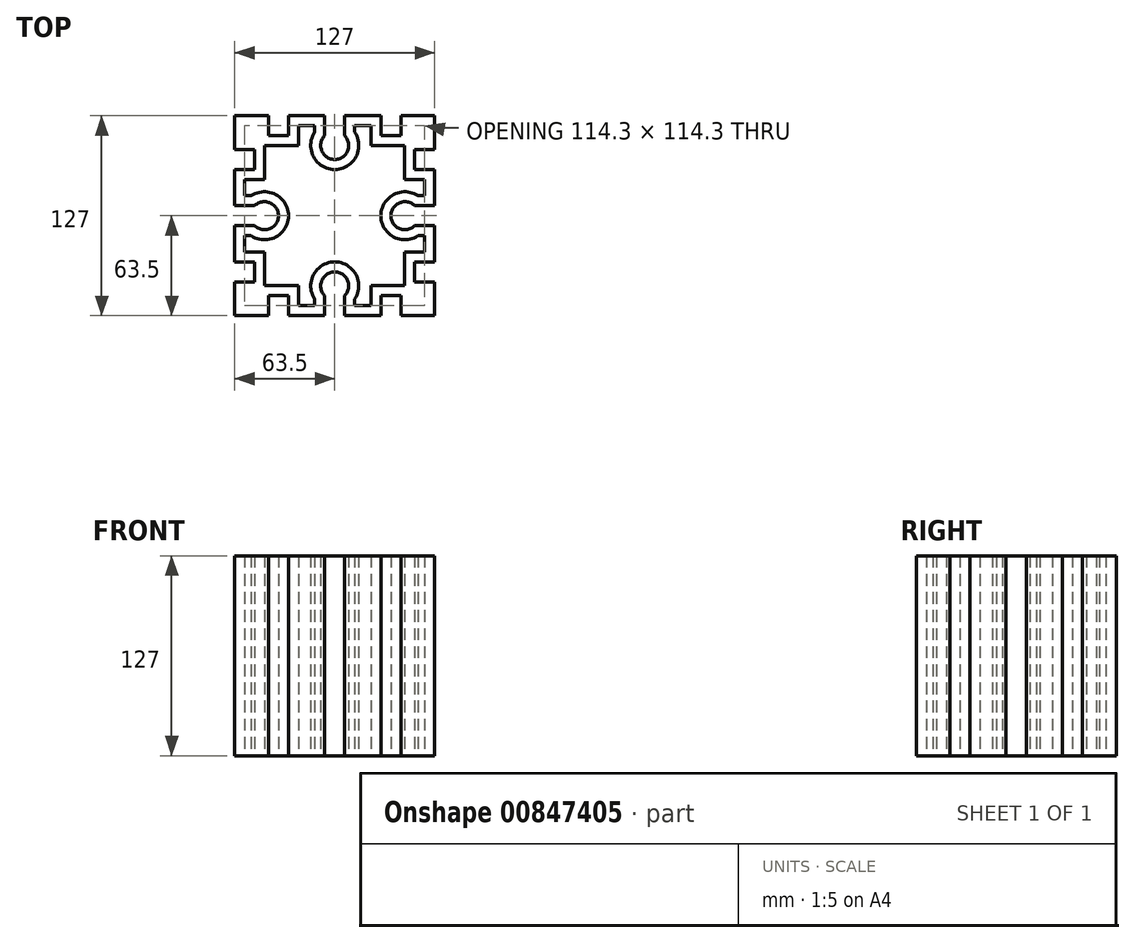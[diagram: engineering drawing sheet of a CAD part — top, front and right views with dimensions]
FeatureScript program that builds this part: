
annotation { "Feature Type Name" : "Feature", "Feature Type Description" : "" }
export const myFeature = defineFeature(function(context is Context, id is Id, definition is map)
    precondition{}
    {
        {
            var Q0;
            Q0=qCreatedBy(makeId("Top.planeOp"),FACE);
            var sketch = newSketch(context, id + "F0", { "sketchPlane" : qUnion([Q0])});
            skLineSegment(sketch, "E0.bottom", {"start": v(-63.5, 63.5) * mm, "end": v(-42.1, 63.5) * mm});
            skLineSegment(sketch, "E0.top", {"start": v(-29.4, -63.5) * mm, "end": v(-6.35, -63.5) * mm});
            skLineSegment(sketch, "E0.right", {"start": v(63.5, 63.5) * mm, "end": v(63.5, 42.1) * mm});
            skPoint(sketch, "E0.middle", {"position": v(0, 0) * mm});
            skLineSegment(sketch, "E1.left", {"start": v(6.35, 50.8) * mm, "end": v(6.35, 63.5) * mm});
            skLineSegment(sketch, "E1.right", {"start": v(-6.35, 50.8) * mm, "end": v(-6.35, 63.5) * mm});
            skPoint(sketch, "E1.middle", {"position": v(0, 63.5) * mm});
            skLineSegment(sketch, "E2.bottom", {"start": v(-29.4, 50.8) * mm, "end": v(-42.1, 50.8) * mm});
            skLineSegment(sketch, "E2.left", {"start": v(-29.4, 50.8) * mm, "end": v(-29.4, 63.5) * mm});
            skLineSegment(sketch, "E2.right", {"start": v(-42.1, 50.8) * mm, "end": v(-42.1, 63.5) * mm});
            skPoint(sketch, "E2.middle", {"position": v(-35.75, 63.5) * mm});
            skPoint(sketch, "E3.MirrorP", {"position": v(0, 127) * mm});
            skLineSegment(sketch, "E4.MirrorCS", {"start": v(29.4, 50.8) * mm, "end": v(42.1, 50.8) * mm});
            skPoint(sketch, "E5.MirrorP", {"position": v(35.75, 63.5) * mm});
            skLineSegment(sketch, "E6.MirrorCS", {"start": v(29.4, 50.8) * mm, "end": v(29.4, 63.5) * mm});
            skLineSegment(sketch, "E7.MirrorCS", {"start": v(42.1, 50.8) * mm, "end": v(42.1, 63.5) * mm});
            skPoint(sketch, "E8.MirrorCS.end.orphan", {"position": v(42.1, 76.2) * mm});
            skPoint(sketch, "E9.orphan", {"position": v(29.4, 76.2) * mm});
            skPoint(sketch, "E1.top.start.orphan", {"position": v(6.35, 76.2) * mm});
            skPoint(sketch, "E10.orphan", {"position": v(-6.35, 76.2) * mm});
            skPoint(sketch, "E11.orphan", {"position": v(-29.4, 76.2) * mm});
            skPoint(sketch, "E12.orphan", {"position": v(-42.1, 76.2) * mm});
            skLineSegment(sketch, "E13.trimOffspring", {"start": v(-29.4, 63.5) * mm, "end": v(-6.35, 63.5) * mm});
            skLineSegment(sketch, "E14.trimOffspring", {"start": v(6.35, 63.5) * mm, "end": v(29.4, 63.5) * mm});
            skLineSegment(sketch, "E15.trimOffspring", {"start": v(42.1, 63.5) * mm, "end": v(63.5, 63.5) * mm});
            skArc(sketch, "E16", {"start": v(-6.35, 50.8) * mm, "mid": v(0, 35.69) * mm, "end": v(6.35, 50.8) * mm});
            skPoint(sketch, "E17.1.0", {"position": v(-76.2, 6.35) * mm});
            skPoint(sketch, "E17.1.1", {"position": v(-76.2, -29.4) * mm});
            skPoint(sketch, "E17.1.2", {"position": v(-76.2, -6.35) * mm});
            skLineSegment(sketch, "E17.1.3", {"start": v(-50.8, 29.4) * mm, "end": v(-50.8, 42.1) * mm});
            skLineSegment(sketch, "E17.1.4", {"start": v(-50.8, -6.35) * mm, "end": v(-63.5, -6.35) * mm});
            skPoint(sketch, "E17.1.5", {"position": v(-76.2, -42.1) * mm});
            skLineSegment(sketch, "E17.1.6", {"start": v(-50.8, 29.4) * mm, "end": v(-63.5, 29.4) * mm});
            skArc(sketch, "E17.1.7", {"start": v(-50.8, -6.35) * mm, "mid": v(-35.69, 0) * mm, "end": v(-50.8, 6.35) * mm});
            skLineSegment(sketch, "E17.1.10", {"start": v(-50.8, 6.35) * mm, "end": v(-63.5, 6.35) * mm});
            skPoint(sketch, "E17.1.11", {"position": v(-76.2, 29.4) * mm});
            skLineSegment(sketch, "E17.1.12", {"start": v(-50.8, -29.4) * mm, "end": v(-63.5, -29.4) * mm});
            skPoint(sketch, "E17.1.13", {"position": v(-76.2, 42.1) * mm});
            skLineSegment(sketch, "E17.1.14", {"start": v(-50.8, 42.1) * mm, "end": v(-63.5, 42.1) * mm});
            skPoint(sketch, "E17.1.15", {"position": v(-63.5, 0) * mm});
            skLineSegment(sketch, "E17.1.16", {"start": v(-50.8, -29.4) * mm, "end": v(-50.8, -42.1) * mm});
            skLineSegment(sketch, "E17.1.17", {"start": v(-50.8, -42.1) * mm, "end": v(-63.5, -42.1) * mm});
            skPoint(sketch, "E17.1.18", {"position": v(-63.5, 35.75) * mm});
            skLineSegment(sketch, "E17.1.19", {"start": v(-63.5, 42.1) * mm, "end": v(-63.5, 63.5) * mm});
            skPoint(sketch, "E17.1.20", {"position": v(-63.5, -35.75) * mm});
            skPoint(sketch, "E17.1.21", {"position": v(-76.2, -42.1) * mm});
            skPoint(sketch, "E17.1.22", {"position": v(-63.5, 35.75) * mm});
            skLineSegment(sketch, "E17.1.23", {"start": v(-50.8, -42.1) * mm, "end": v(-63.5, -42.1) * mm});
            skLineSegment(sketch, "E17.1.24", {"start": v(-50.8, -42.1) * mm, "end": v(-63.5, -42.1) * mm});
            skPoint(sketch, "E17.1.25", {"position": v(-76.2, -42.1) * mm});
            skPoint(sketch, "E17.2.0", {"position": v(-6.35, -76.2) * mm});
            skPoint(sketch, "E17.2.1", {"position": v(29.4, -76.2) * mm});
            skPoint(sketch, "E17.2.2", {"position": v(6.35, -76.2) * mm});
            skLineSegment(sketch, "E17.2.3", {"start": v(-29.4, -50.8) * mm, "end": v(-42.1, -50.8) * mm});
            skLineSegment(sketch, "E17.2.4", {"start": v(6.35, -50.8) * mm, "end": v(6.35, -63.5) * mm});
            skPoint(sketch, "E17.2.5", {"position": v(42.1, -76.2) * mm});
            skLineSegment(sketch, "E17.2.6", {"start": v(-29.4, -50.8) * mm, "end": v(-29.4, -63.5) * mm});
            skArc(sketch, "E17.2.7", {"start": v(6.35, -50.8) * mm, "mid": v(0, -35.69) * mm, "end": v(-6.35, -50.8) * mm});
            skLineSegment(sketch, "E17.2.10", {"start": v(-6.35, -50.8) * mm, "end": v(-6.35, -63.5) * mm});
            skPoint(sketch, "E17.2.11", {"position": v(-29.4, -76.2) * mm});
            skLineSegment(sketch, "E17.2.12", {"start": v(29.4, -50.8) * mm, "end": v(29.4, -63.5) * mm});
            skPoint(sketch, "E17.2.13", {"position": v(-42.1, -76.2) * mm});
            skLineSegment(sketch, "E17.2.14", {"start": v(-42.1, -50.8) * mm, "end": v(-42.1, -63.5) * mm});
            skPoint(sketch, "E17.2.15", {"position": v(0, -63.5) * mm});
            skLineSegment(sketch, "E17.2.16", {"start": v(29.4, -50.8) * mm, "end": v(42.1, -50.8) * mm});
            skLineSegment(sketch, "E17.2.17", {"start": v(42.1, -50.8) * mm, "end": v(42.1, -63.5) * mm});
            skPoint(sketch, "E17.2.18", {"position": v(-35.75, -63.5) * mm});
            skLineSegment(sketch, "E17.2.19", {"start": v(-42.1, -63.5) * mm, "end": v(-63.5, -63.5) * mm});
            skPoint(sketch, "E17.2.20", {"position": v(35.75, -63.5) * mm});
            skPoint(sketch, "E17.2.21", {"position": v(42.1, -76.2) * mm});
            skPoint(sketch, "E17.2.22", {"position": v(-35.75, -63.5) * mm});
            skLineSegment(sketch, "E17.2.23", {"start": v(42.1, -50.8) * mm, "end": v(42.1, -63.5) * mm});
            skLineSegment(sketch, "E17.2.24", {"start": v(42.1, -50.8) * mm, "end": v(42.1, -63.5) * mm});
            skPoint(sketch, "E17.2.25", {"position": v(42.1, -76.2) * mm});
            skPoint(sketch, "E17.3.0", {"position": v(76.2, -6.35) * mm});
            skPoint(sketch, "E17.3.1", {"position": v(76.2, 29.4) * mm});
            skPoint(sketch, "E17.3.2", {"position": v(76.2, 6.35) * mm});
            skLineSegment(sketch, "E17.3.3", {"start": v(50.8, -29.4) * mm, "end": v(50.8, -42.1) * mm});
            skLineSegment(sketch, "E17.3.4", {"start": v(50.8, 6.35) * mm, "end": v(63.5, 6.35) * mm});
            skPoint(sketch, "E17.3.5", {"position": v(76.2, 42.1) * mm});
            skLineSegment(sketch, "E17.3.6", {"start": v(50.8, -29.4) * mm, "end": v(63.5, -29.4) * mm});
            skArc(sketch, "E17.3.7", {"start": v(50.8, 6.35) * mm, "mid": v(35.69, 0) * mm, "end": v(50.8, -6.35) * mm});
            skLineSegment(sketch, "E17.3.8", {"start": v(63.5, -6.35) * mm, "end": v(63.5, -29.4) * mm});
            skLineSegment(sketch, "E17.3.9", {"start": v(63.5, 29.4) * mm, "end": v(63.5, 6.35) * mm});
            skLineSegment(sketch, "E17.3.10", {"start": v(50.8, -6.35) * mm, "end": v(63.5, -6.35) * mm});
            skPoint(sketch, "E17.3.11", {"position": v(76.2, -29.4) * mm});
            skLineSegment(sketch, "E17.3.12", {"start": v(50.8, 29.4) * mm, "end": v(63.5, 29.4) * mm});
            skPoint(sketch, "E17.3.13", {"position": v(76.2, -42.1) * mm});
            skLineSegment(sketch, "E17.3.14", {"start": v(50.8, -42.1) * mm, "end": v(63.5, -42.1) * mm});
            skPoint(sketch, "E17.3.15", {"position": v(63.5, 0) * mm});
            skLineSegment(sketch, "E17.3.16", {"start": v(50.8, 29.4) * mm, "end": v(50.8, 42.1) * mm});
            skLineSegment(sketch, "E17.3.17", {"start": v(50.8, 42.1) * mm, "end": v(63.5, 42.1) * mm});
            skPoint(sketch, "E17.3.18", {"position": v(63.5, -35.75) * mm});
            skLineSegment(sketch, "E17.3.19", {"start": v(63.5, -42.1) * mm, "end": v(63.5, -63.5) * mm});
            skPoint(sketch, "E17.3.20", {"position": v(63.5, 35.75) * mm});
            skPoint(sketch, "E17.3.21", {"position": v(76.2, 42.1) * mm});
            skPoint(sketch, "E17.3.22", {"position": v(63.5, -35.75) * mm});
            skLineSegment(sketch, "E17.3.23", {"start": v(50.8, 42.1) * mm, "end": v(63.5, 42.1) * mm});
            skLineSegment(sketch, "E17.3.24", {"start": v(50.8, 42.1) * mm, "end": v(63.5, 42.1) * mm});
            skPoint(sketch, "E17.3.25", {"position": v(76.2, 42.1) * mm});
            skLineSegment(sketch, "E18.trimOffspring", {"start": v(-63.5, 29.4) * mm, "end": v(-63.5, 6.35) * mm});
            skLineSegment(sketch, "E19.trimOffspring", {"start": v(-63.5, -6.35) * mm, "end": v(-63.5, -29.4) * mm});
            skLineSegment(sketch, "E20.trimOffspring", {"start": v(-63.5, -42.1) * mm, "end": v(-63.5, -63.5) * mm});
            skLineSegment(sketch, "E21.trimOffspring", {"start": v(6.35, -63.5) * mm, "end": v(29.4, -63.5) * mm});
            skLineSegment(sketch, "E22.trimOffspring", {"start": v(42.1, -63.5) * mm, "end": v(63.5, -63.5) * mm});
            skLineSegment(sketch, "E23.0", {"start": v(-44.45, 23.05) * mm, "end": v(-44.45, 44.45) * mm});
            skLineSegment(sketch, "E23.1", {"start": v(-44.45, 23.05) * mm, "end": v(-57.15, 23.05) * mm});
            skLineSegment(sketch, "E23.2", {"start": v(-57.15, 23.05) * mm, "end": v(-57.15, 12.7) * mm});
            skLineSegment(sketch, "E23.3", {"start": v(-53, 12.7) * mm, "end": v(-57.15, 12.7) * mm});
            skArc(sketch, "E23.4", {"start": v(-53, -12.7) * mm, "mid": v(-29.34, 0) * mm, "end": v(-53, 12.7) * mm});
            skLineSegment(sketch, "E23.5", {"start": v(-44.45, -23.05) * mm, "end": v(-44.45, -44.45) * mm});
            skLineSegment(sketch, "E23.6", {"start": v(-44.45, -23.05) * mm, "end": v(-57.15, -23.05) * mm});
            skLineSegment(sketch, "E23.7", {"start": v(-57.15, -12.7) * mm, "end": v(-57.15, -23.05) * mm});
            skLineSegment(sketch, "E23.8", {"start": v(-53, -12.7) * mm, "end": v(-57.15, -12.7) * mm});
            skLineSegment(sketch, "E24.1.0", {"start": v(12.7, 53) * mm, "end": v(12.7, 57.15) * mm});
            skArc(sketch, "E24.1.1", {"start": v(-12.7, 53) * mm, "mid": v(0, 29.34) * mm, "end": v(12.7, 53) * mm});
            skLineSegment(sketch, "E24.1.2", {"start": v(-12.7, 53) * mm, "end": v(-12.7, 57.15) * mm});
            skLineSegment(sketch, "E24.1.3", {"start": v(-12.7, 57.15) * mm, "end": v(-23.05, 57.15) * mm});
            skLineSegment(sketch, "E24.1.4", {"start": v(-23.05, 44.45) * mm, "end": v(-23.05, 57.15) * mm});
            skLineSegment(sketch, "E24.1.5", {"start": v(-23.05, 44.45) * mm, "end": v(-44.45, 44.45) * mm});
            skLineSegment(sketch, "E24.1.6", {"start": v(23.05, 57.15) * mm, "end": v(12.7, 57.15) * mm});
            skLineSegment(sketch, "E24.1.7", {"start": v(23.05, 44.45) * mm, "end": v(23.05, 57.15) * mm});
            skLineSegment(sketch, "E24.1.8", {"start": v(23.05, 44.45) * mm, "end": v(44.45, 44.45) * mm});
            skLineSegment(sketch, "E24.2.0", {"start": v(53, -12.7) * mm, "end": v(57.15, -12.7) * mm});
            skArc(sketch, "E24.2.1", {"start": v(53, 12.7) * mm, "mid": v(29.34, 0) * mm, "end": v(53, -12.7) * mm});
            skLineSegment(sketch, "E24.2.2", {"start": v(53, 12.7) * mm, "end": v(57.15, 12.7) * mm});
            skLineSegment(sketch, "E24.2.3", {"start": v(57.15, 12.7) * mm, "end": v(57.15, 23.05) * mm});
            skLineSegment(sketch, "E24.2.4", {"start": v(44.45, 23.05) * mm, "end": v(57.15, 23.05) * mm});
            skLineSegment(sketch, "E24.2.5", {"start": v(44.45, 23.05) * mm, "end": v(44.45, 44.45) * mm});
            skLineSegment(sketch, "E24.2.6", {"start": v(57.15, -23.05) * mm, "end": v(57.15, -12.7) * mm});
            skLineSegment(sketch, "E24.2.7", {"start": v(44.45, -23.05) * mm, "end": v(57.15, -23.05) * mm});
            skLineSegment(sketch, "E24.2.8", {"start": v(44.45, -23.05) * mm, "end": v(44.45, -44.45) * mm});
            skLineSegment(sketch, "E24.3.0", {"start": v(-12.7, -53) * mm, "end": v(-12.7, -57.15) * mm});
            skArc(sketch, "E24.3.1", {"start": v(12.7, -53) * mm, "mid": v(0, -29.34) * mm, "end": v(-12.7, -53) * mm});
            skLineSegment(sketch, "E24.3.2", {"start": v(12.7, -53) * mm, "end": v(12.7, -57.15) * mm});
            skLineSegment(sketch, "E24.3.3", {"start": v(12.7, -57.15) * mm, "end": v(23.05, -57.15) * mm});
            skLineSegment(sketch, "E24.3.4", {"start": v(23.05, -44.45) * mm, "end": v(23.05, -57.15) * mm});
            skLineSegment(sketch, "E24.3.5", {"start": v(23.05, -44.45) * mm, "end": v(44.45, -44.45) * mm});
            skLineSegment(sketch, "E24.3.6", {"start": v(-23.05, -57.15) * mm, "end": v(-12.7, -57.15) * mm});
            skLineSegment(sketch, "E24.3.7", {"start": v(-23.05, -44.45) * mm, "end": v(-23.05, -57.15) * mm});
            skLineSegment(sketch, "E24.3.8", {"start": v(-23.05, -44.45) * mm, "end": v(-44.45, -44.45) * mm});
            skLineSegment(sketch, "E24.anchor1", {"start": v(0, 0) * mm, "end": v(-57.15, 12.7) * mm, "construction": true});
            skLineSegment(sketch, "E24.anchor2", {"start": v(0, 0) * mm, "end": v(-12.7, -57.15) * mm, "construction": true});
            skPoint(sketch, "E25.orphan", {"position": v(44.45, 42.1) * mm});
            skPoint(sketch, "E26.orphan", {"position": v(42.1, 44.45) * mm});
            skPoint(sketch, "E27.orphan", {"position": v(-42.1, -44.45) * mm});
            skPoint(sketch, "E28.orphan", {"position": v(-44.45, -42.1) * mm});
            skPoint(sketch, "E29.orphan", {"position": v(-42.1, 44.45) * mm});
            skPoint(sketch, "E30.orphan", {"position": v(-44.45, 42.1) * mm});
            skPoint(sketch, "E31.orphan", {"position": v(44.45, -42.1) * mm});
            skPoint(sketch, "E32.orphan", {"position": v(42.1, -44.45) * mm});
            skSolve(sketch);
        }
        {
            var Q0;
            Q0=makeQuery(id+"F0.imprint","IMPRINT",FACE,{"disambiguationData":[TD([[makeQuery(id+"F0.imprint","IMPRINT",EDGE,{"derivedFrom":sQuery(id+"F0.wireOp",EDGE,"E0.bottom")}),-1.0]])]});
            extrude(context, id + "F1", {"entities" : qUnion([Q0]), "depth" : 127 * mm, "offsetDistance" : 25.4 * mm});
        }
    });
